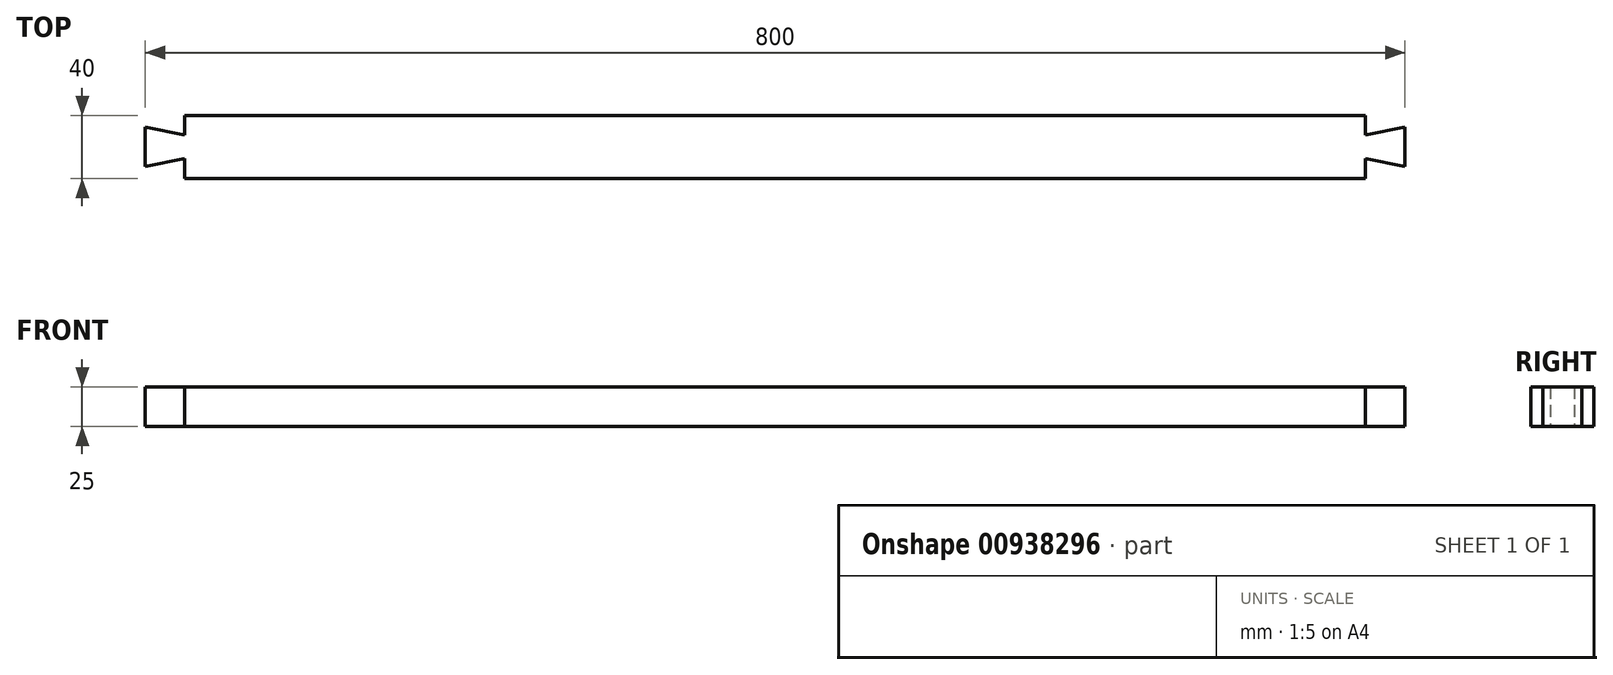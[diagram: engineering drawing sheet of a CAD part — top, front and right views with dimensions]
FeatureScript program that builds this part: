
annotation { "Feature Type Name" : "Feature", "Feature Type Description" : "" }
export const myFeature = defineFeature(function(context is Context, id is Id, definition is map)
    precondition{}
    {
        {
            var Q0;
            Q0=qCreatedBy(makeId("Top.planeOp"),FACE);
            var sketch = newSketch(context, id + "F0", { "sketchPlane" : qUnion([Q0])});
            skLineSegment(sketch, "E0.bottom", {"start": v(-106.76, 17.8) * mm, "end": v(643.24, 17.8) * mm});
            skLineSegment(sketch, "E0.top", {"start": v(-106.76, -22.2) * mm, "end": v(643.24, -22.2) * mm});
            skLineSegment(sketch, "E0.left", {"start": v(-106.76, 17.8) * mm, "end": v(-106.76, -22.2) * mm});
            skLineSegment(sketch, "E0.right", {"start": v(643.24, 17.8) * mm, "end": v(643.24, -22.2) * mm});
            skLineSegment(sketch, "E1", {"start": v(-106.76, 5.3) * mm, "end": v(-106.76, -9.7) * mm});
            skLineSegment(sketch, "E2", {"start": v(-106.76, -9.7) * mm, "end": v(-131.76, -14.7) * mm});
            skLineSegment(sketch, "E3", {"start": v(-131.76, -14.7) * mm, "end": v(-131.76, 10.3) * mm});
            skLineSegment(sketch, "E4", {"start": v(-131.76, 10.3) * mm, "end": v(-106.76, 5.3) * mm});
            skSolve(sketch);
        }
        {
            var Q0;
            {var subQ3=sQuery(id+"F0.wireOp",EDGE,"E2");var subQ6=sQuery(id+"F0.wireOp",EDGE,"E0.bottom");Q0=qUnion([makeQuery(id+"F0.imprint","IMPRINT",FACE,{"disambiguationData":[TD([[makeQuery(id+"F0.imprint","IMPRINT",EDGE,{"derivedFrom":subQ6}),-1.0]])]}),makeQuery(id+"F0.imprint","IMPRINT",FACE,{"disambiguationData":[TD([[makeQuery(id+"F0.imprint","IMPRINT",EDGE,{"derivedFrom":subQ3}),-1.0]])]})]);}
            extrude(context, id + "F1", {"entities" : qUnion([Q0]), "depth" : 25 * mm, "offsetDistance" : 25 * mm});
        }
        {
            var Q0;
            Q0=makeQuery(id+"F1.opExtrude","CAP_EDGE",EDGE,{"disambiguationData":[OSD([sQuery(id+"F0.wireOp",EDGE,"E0.top")])],"isStart":false});
            cPoint(context, id + "F2", {"entities" : qUnion([Q0]), "parameter" : 0.5});
        }
        {
            var Q0;
            Q0=makeQuery(id+"F1.opExtrude","CAP_EDGE",EDGE,{"disambiguationData":[OSD([sQuery(id+"F0.wireOp",EDGE,"E0.bottom")])],"isStart":false});
            cPoint(context, id + "F3", {"entities" : qUnion([Q0]), "parameter" : 0.5});
        }
        {
            var Q0;
            Q0=makeQuery(id+"F1.opExtrude","CAP_EDGE",EDGE,{"disambiguationData":[OSD([sQuery(id+"F0.wireOp",EDGE,"E0.bottom")])],"isStart":true});
            cPoint(context, id + "F4", {"entities" : qUnion([Q0]), "parameter" : 0.5});
        }
        {
            var Q0;
            Q0 = qCreatedBy(id + "F2" ,VERTEX);
            var Q1;
            Q1 = qCreatedBy(id + "F3" ,VERTEX);
            var Q2;
            Q2 = qCreatedBy(id + "F4" ,VERTEX);
            cPlane(context, id + "F5", {"entities" : qUnion([Q0, Q1, Q2]), "cplaneType" : CPlaneType.THREE_POINT, "offset" : 25 * mm, "width" : 150 * mm, "height" : 150 * mm});
        }
        {
            var Q0;
            Q0=makeQuery(id+"F1.opExtrude","SWEPT_BODY",BODY,{"disambiguationData":[OSD([sQuery(id+"F0.wireOp",EDGE,"E0.bottom"),sQuery(id+"F0.wireOp",EDGE,"E0.top"),sQuery(id+"F0.wireOp",EDGE,"E0.left"),sQuery(id+"F0.wireOp",EDGE,"E0.right"),sQuery(id+"F0.wireOp",EDGE,"E2"),sQuery(id+"F0.wireOp",EDGE,"E3"),sQuery(id+"F0.wireOp",EDGE,"E4")])]});
            var Q1;
            Q1=qCreatedBy(id+"F5.planeOp",FACE);
            mirror(context, id + "F6", {"operationType" : NewBodyOperationType.ADD, "entities" : qUnion([Q0]), "mirrorPlane" : qUnion([Q1])});
        }
    });
